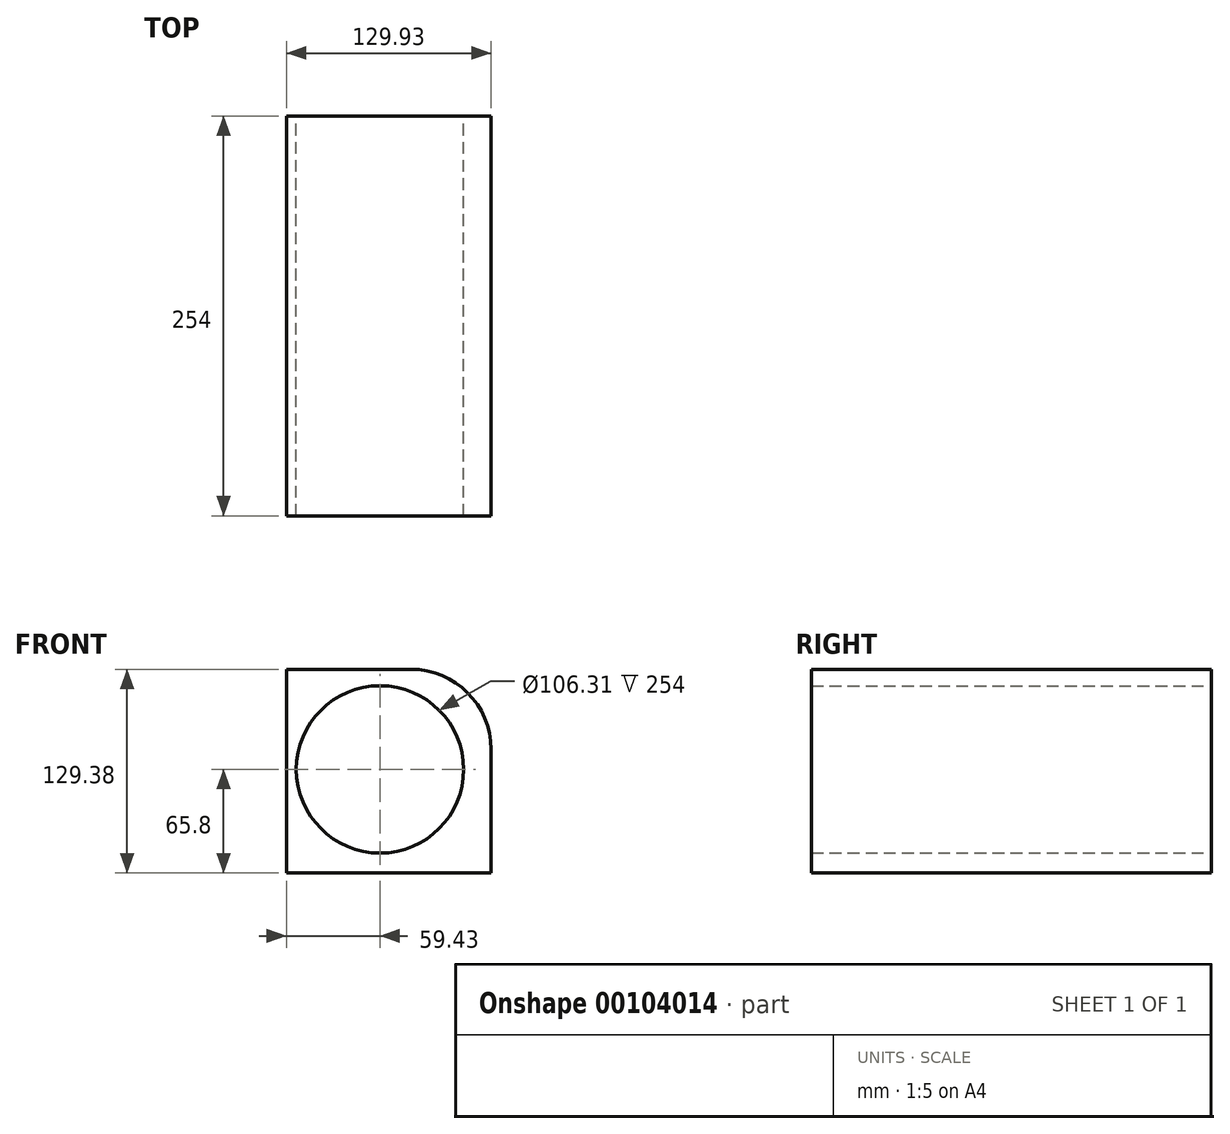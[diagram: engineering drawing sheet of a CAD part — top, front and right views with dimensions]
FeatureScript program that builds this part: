
annotation { "Feature Type Name" : "Feature", "Feature Type Description" : "" }
export const myFeature = defineFeature(function(context is Context, id is Id, definition is map)
    precondition{}
    {
        {
            var Q0;
            Q0=qCreatedBy(makeId("Front.planeOp"),FACE);
            var sketch = newSketch(context, id + "F0", { "sketchPlane" : qUnion([Q0])});
            skCircle(sketch, "E0", {"center": v(0, 0) * mm, "radius": 53.16 * mm});
            skLineSegment(sketch, "E1.bottom", {"start": v(-59.43, 63.58) * mm, "end": v(70.5, 63.58) * mm});
            skLineSegment(sketch, "E1.top", {"start": v(-59.43, -65.8) * mm, "end": v(70.5, -65.8) * mm});
            skLineSegment(sketch, "E1.left", {"start": v(-59.43, 63.58) * mm, "end": v(-59.43, -65.8) * mm});
            skLineSegment(sketch, "E1.right", {"start": v(70.5, 63.58) * mm, "end": v(70.5, -65.8) * mm});
            skSolve(sketch);
        }
        {
            var Q0;
            Q0=makeQuery(id+"F0.imprint","IMPRINT",FACE,{"disambiguationData":[TD([[makeQuery(id+"F0.imprint","IMPRINT",EDGE,{"derivedFrom":sQuery(id+"F0.wireOp",EDGE,"E0")}),-1.0]])]});
            extrude(context, id + "F1", {"entities" : qUnion([Q0]), "depth" : 254 * mm});
        }
        {
            var Q0;
            Q0=makeQuery(id+"F1.opExtrude","SWEPT_EDGE",EDGE,{"disambiguationData":[OSD([sQuery(id+"F0.wireOp",EDGE,"E1.bottom"),sQuery(id+"F0.wireOp",EDGE,"E1.right")])]});
            fillet(context, id + "F2", {"entities" : qUnion([Q0]), "radius" : 50.8 * mm, "tangentPropagation" : true, "allowEdgeOverflow" : false});
        }
    });
